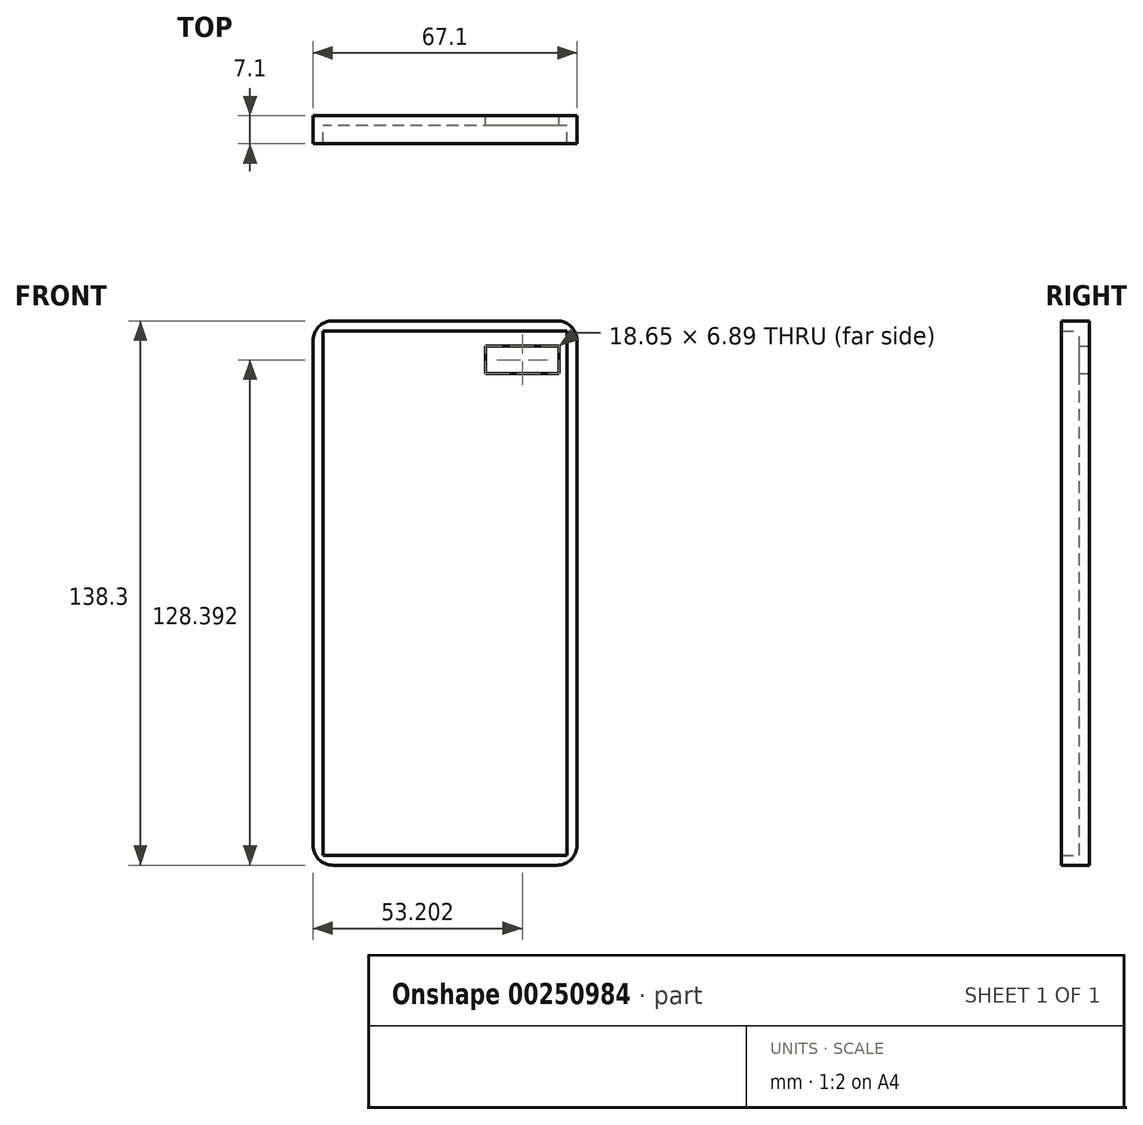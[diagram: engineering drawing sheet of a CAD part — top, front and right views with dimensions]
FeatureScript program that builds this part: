
annotation { "Feature Type Name" : "Feature", "Feature Type Description" : "" }
export const myFeature = defineFeature(function(context is Context, id is Id, definition is map)
    precondition{}
    {
        {
            var Q0;
            Q0=qCreatedBy(makeId("Front.planeOp"),FACE);
            var sketch = newSketch(context, id + "F0", { "sketchPlane" : qUnion([Q0])});
            skLineSegment(sketch, "E0.bottom", {"start": v(33.55, -69.15) * mm, "end": v(-33.55, -69.15) * mm});
            skLineSegment(sketch, "E0.top", {"start": v(33.55, 69.15) * mm, "end": v(-33.55, 69.15) * mm});
            skLineSegment(sketch, "E0.left", {"start": v(33.55, -69.15) * mm, "end": v(33.55, 69.15) * mm});
            skLineSegment(sketch, "E0.right", {"start": v(-33.55, -69.15) * mm, "end": v(-33.55, 69.15) * mm});
            skPoint(sketch, "E0.middle", {"position": v(0, 0) * mm});
            skSolve(sketch);
        }
        {
            var Q0;
            Q0=makeQuery(id+"F0.imprint","IMPRINT",FACE,{"disambiguationData":[TD([[makeQuery(id+"F0.imprint","IMPRINT",EDGE,{"derivedFrom":sQuery(id+"F0.wireOp",EDGE,"E0.bottom")}),-1.0]])]});
            extrude(context, id + "F1", {"entities" : qUnion([Q0]), "endBound" : BoundingType.SYMMETRIC, "depth" : 7.1 * mm});
        }
        {
            var Q0;
            Q0=makeQuery(id+"F1.opExtrude","CAP_FACE",FACE,{"disambiguationData":[OSD([sQuery(id+"F0.wireOp",EDGE,"E0.bottom"),sQuery(id+"F0.wireOp",EDGE,"E0.top"),sQuery(id+"F0.wireOp",EDGE,"E0.left"),sQuery(id+"F0.wireOp",EDGE,"E0.right")])],"isStart":false});
            shell(context, id + "F2", {"entities" : qUnion([Q0]), "thickness" : 2.54 * mm});
        }
        {
            var Q0;
            Q0=makeQuery(id+"F1.opExtrude","SWEPT_EDGE",EDGE,{"disambiguationData":[OSD([sQuery(id+"F0.wireOp",EDGE,"E0.top"),sQuery(id+"F0.wireOp",EDGE,"E0.left")])]});
            var Q1;
            Q1=makeQuery(id+"F1.opExtrude","SWEPT_EDGE",EDGE,{"disambiguationData":[OSD([sQuery(id+"F0.wireOp",EDGE,"E0.top"),sQuery(id+"F0.wireOp",EDGE,"E0.right")])]});
            var Q2;
            Q2=makeQuery(id+"F1.opExtrude","SWEPT_EDGE",EDGE,{"disambiguationData":[OSD([sQuery(id+"F0.wireOp",EDGE,"E0.bottom"),sQuery(id+"F0.wireOp",EDGE,"E0.right")])]});
            var Q3;
            Q3=makeQuery(id+"F1.opExtrude","SWEPT_EDGE",EDGE,{"disambiguationData":[OSD([sQuery(id+"F0.wireOp",EDGE,"E0.bottom"),sQuery(id+"F0.wireOp",EDGE,"E0.left")])]});
            fillet(context, id + "F3", {"entities" : qUnion([Q0, Q1, Q2, Q3]), "radius" : 5.08 * mm, "tangentPropagation" : true, "allowEdgeOverflow" : false});
        }
        {
            var Q0;
            Q0=qCreatedBy(makeId("Front.planeOp"),FACE);
            var sketch = newSketch(context, id + "F4", { "sketchPlane" : qUnion([Q0])});
            skLineSegment(sketch, "E1.bottom", {"start": v(10.33, 62.68) * mm, "end": v(28.98, 62.68) * mm});
            skLineSegment(sketch, "E1.top", {"start": v(10.33, 55.8) * mm, "end": v(28.98, 55.8) * mm});
            skLineSegment(sketch, "E1.left", {"start": v(10.33, 62.68) * mm, "end": v(10.33, 55.8) * mm});
            skLineSegment(sketch, "E1.right", {"start": v(28.98, 62.68) * mm, "end": v(28.98, 55.8) * mm});
            skSolve(sketch);
        }
        {
            var Q0;
            Q0=makeQuery(id+"F4.imprint","IMPRINT",FACE,{"disambiguationData":[TD([[makeQuery(id+"F4.imprint","IMPRINT",EDGE,{"derivedFrom":sQuery(id+"F4.wireOp",EDGE,"E1.bottom")}),-1.0]])]});
            extrude(context, id + "F5", {"entities" : qUnion([Q0]), "operationType" : NewBodyOperationType.REMOVE, "endBound" : BoundingType.SYMMETRIC, "depth" : 25 * mm});
        }
    });
